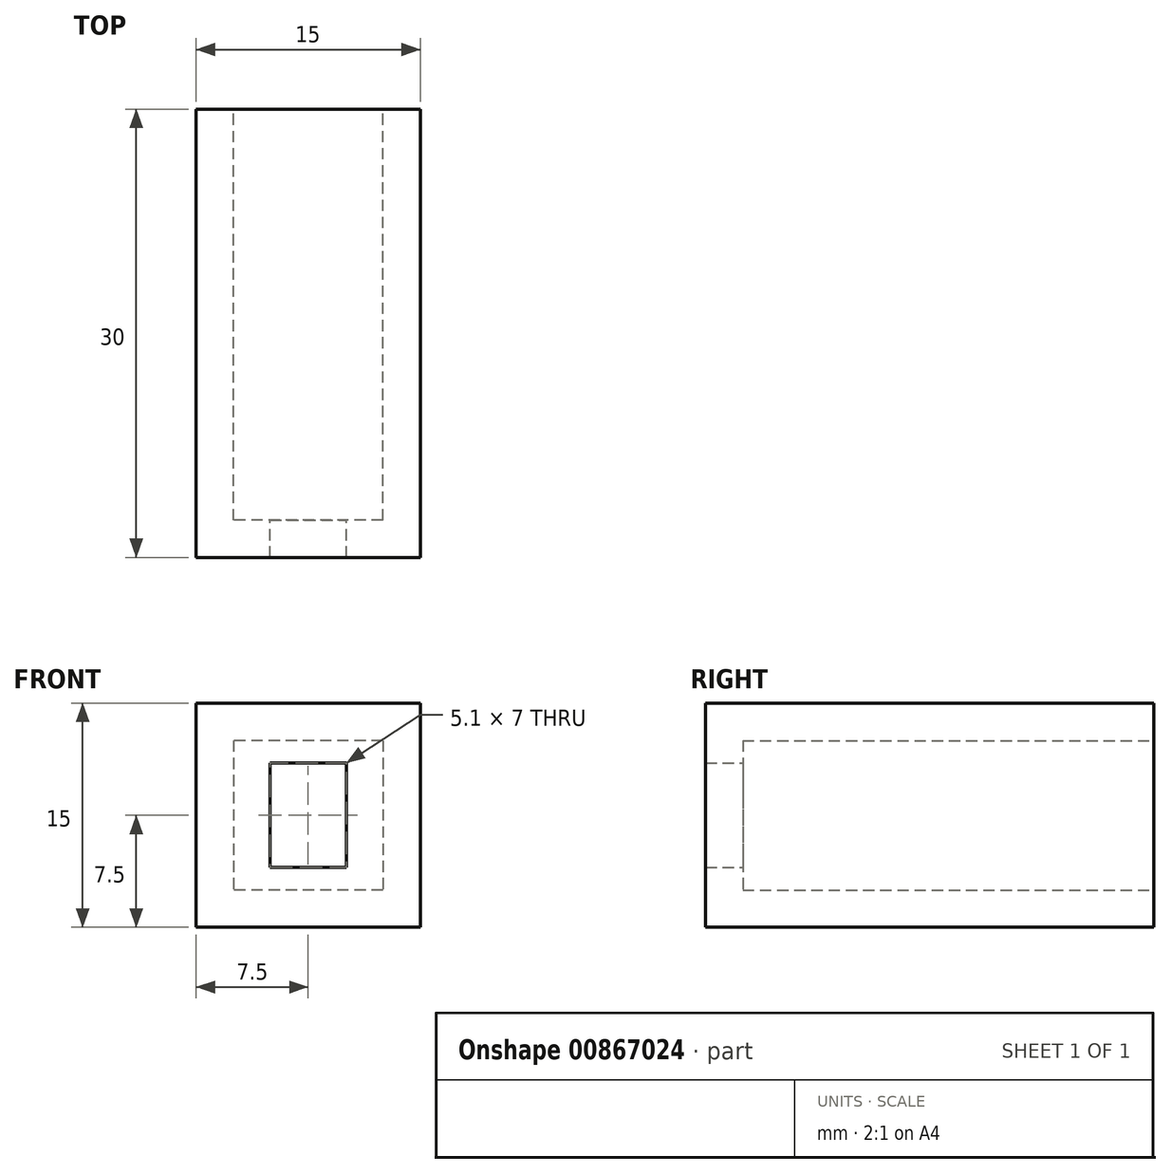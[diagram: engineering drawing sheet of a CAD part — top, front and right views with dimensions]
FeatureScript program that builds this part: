
annotation { "Feature Type Name" : "Feature", "Feature Type Description" : "" }
export const myFeature = defineFeature(function(context is Context, id is Id, definition is map)
    precondition{}
    {
        {
            var Q0;
            Q0=qCreatedBy(makeId("Front.planeOp"),FACE);
            var sketch = newSketch(context, id + "F0", { "sketchPlane" : qUnion([Q0])});
            skLineSegment(sketch, "E0.bottom", {"start": v(7.5, 7.5) * mm, "end": v(-7.5, 7.5) * mm});
            skLineSegment(sketch, "E0.top", {"start": v(7.5, -7.5) * mm, "end": v(-7.5, -7.5) * mm});
            skLineSegment(sketch, "E0.left", {"start": v(7.5, 7.5) * mm, "end": v(7.5, -7.5) * mm});
            skLineSegment(sketch, "E0.right", {"start": v(-7.5, 7.5) * mm, "end": v(-7.5, -7.5) * mm});
            skLineSegment(sketch, "E1.bottom", {"start": v(-2.55, 3.5) * mm, "end": v(2.55, 3.5) * mm});
            skLineSegment(sketch, "E1.top", {"start": v(-2.55, -3.5) * mm, "end": v(2.55, -3.5) * mm});
            skLineSegment(sketch, "E1.left", {"start": v(-2.55, 3.5) * mm, "end": v(-2.55, -3.5) * mm});
            skLineSegment(sketch, "E1.right", {"start": v(2.55, 3.5) * mm, "end": v(2.55, -3.5) * mm});
            skSolve(sketch);
        }
        {
            var Q0;
            Q0 = qSketchRegion(id + "F0", true);
            extrude(context, id + "F1", {"entities" : qUnion([Q0]), "depth" : 30 * mm, "offsetDistance" : 25 * mm});
        }
        {
            var Q0;
            Q0=makeQuery(id+"F1.opExtrude","CAP_FACE",FACE,{"disambiguationData":[OSD([sQuery(id+"F0.wireOp",EDGE,"E0.bottom"),sQuery(id+"F0.wireOp",EDGE,"E0.top"),sQuery(id+"F0.wireOp",EDGE,"E0.left"),sQuery(id+"F0.wireOp",EDGE,"E0.right"),sQuery(id+"F0.wireOp",EDGE,"E1.bottom"),sQuery(id+"F0.wireOp",EDGE,"E1.top"),sQuery(id+"F0.wireOp",EDGE,"E1.left"),sQuery(id+"F0.wireOp",EDGE,"E1.right")])],"isStart":true});
            var Q1;
            Q1=makeQuery(id+"F1.opExtrude","SWEPT_FACE",FACE,{"disambiguationData":[OSD([sQuery(id+"F0.wireOp",EDGE,"E1.top")])]});
            var Q2;
            Q2=makeQuery(id+"F1.opExtrude","SWEPT_FACE",FACE,{"disambiguationData":[OSD([sQuery(id+"F0.wireOp",EDGE,"E1.right")])]});
            var Q3;
            Q3=makeQuery(id+"F1.opExtrude","SWEPT_FACE",FACE,{"disambiguationData":[OSD([sQuery(id+"F0.wireOp",EDGE,"E1.left")])]});
            var Q4;
            Q4=makeQuery(id+"F1.opExtrude","SWEPT_FACE",FACE,{"disambiguationData":[OSD([sQuery(id+"F0.wireOp",EDGE,"E1.bottom")])]});
            shell(context, id + "F2", {"entities" : qUnion([Q0, Q1, Q2, Q3, Q4]), "thickness" : 2.5 * mm});
        }
    });
